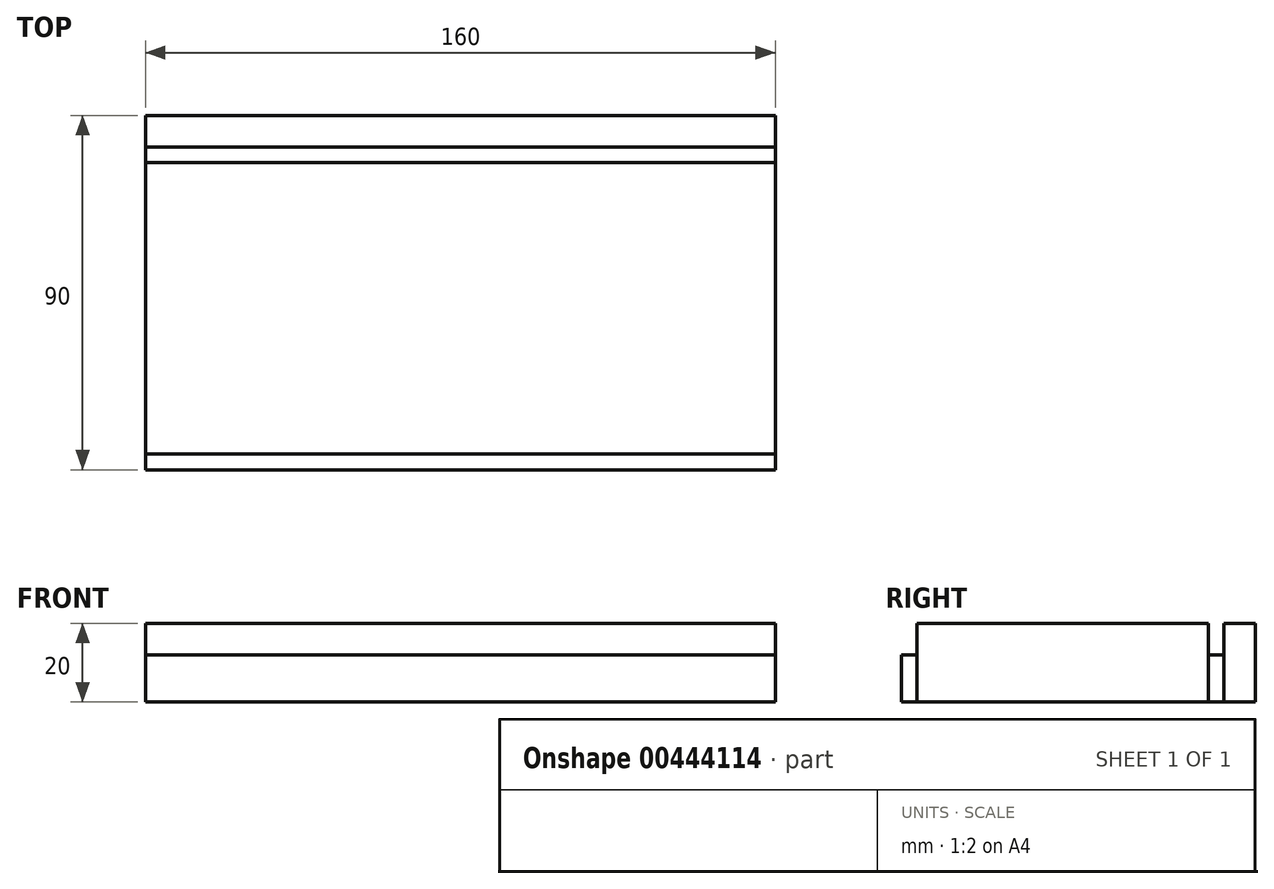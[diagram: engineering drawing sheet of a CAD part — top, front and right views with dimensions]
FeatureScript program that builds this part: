
annotation { "Feature Type Name" : "Feature", "Feature Type Description" : "" }
export const myFeature = defineFeature(function(context is Context, id is Id, definition is map)
    precondition{}
    {
        {
            var Q0;
            Q0=qCreatedBy(makeId("Top.planeOp"),FACE);
            var sketch = newSketch(context, id + "F0", { "sketchPlane" : qUnion([Q0])});
            skLineSegment(sketch, "E0.bottom", {"start": v(-78.73, 59.32) * mm, "end": v(81.27, 59.32) * mm});
            skLineSegment(sketch, "E0.top", {"start": v(-78.73, -30.68) * mm, "end": v(81.27, -30.68) * mm});
            skLineSegment(sketch, "E0.left", {"start": v(-78.73, 59.32) * mm, "end": v(-78.73, -30.68) * mm});
            skLineSegment(sketch, "E0.right", {"start": v(81.27, 59.32) * mm, "end": v(81.27, -30.68) * mm});
            skLineSegment(sketch, "E1.top", {"start": v(-78.73, 51.32) * mm, "end": v(81.27, 51.32) * mm});
            skLineSegment(sketch, "E1.left", {"start": v(-78.73, 59.32) * mm, "end": v(-78.73, 51.32) * mm});
            skLineSegment(sketch, "E1.right", {"start": v(81.27, 59.32) * mm, "end": v(81.27, 51.32) * mm});
            skLineSegment(sketch, "E2.top", {"start": v(-78.73, 47.32) * mm, "end": v(81.27, 47.32) * mm});
            skLineSegment(sketch, "E2.left", {"start": v(-78.73, 51.32) * mm, "end": v(-78.73, 47.32) * mm});
            skLineSegment(sketch, "E2.right", {"start": v(81.27, 51.32) * mm, "end": v(81.27, 47.32) * mm});
            skLineSegment(sketch, "E3.top", {"start": v(-78.73, -26.68) * mm, "end": v(81.27, -26.68) * mm});
            skLineSegment(sketch, "E3.left", {"start": v(-78.73, 47.32) * mm, "end": v(-78.73, -26.68) * mm});
            skLineSegment(sketch, "E3.right", {"start": v(81.27, 47.32) * mm, "end": v(81.27, -26.68) * mm});
            skLineSegment(sketch, "E4.left", {"start": v(-78.73, -26.68) * mm, "end": v(-78.73, -30.68) * mm});
            skLineSegment(sketch, "E4.right", {"start": v(81.27, -26.68) * mm, "end": v(81.27, -30.68) * mm});
            skSolve(sketch);
        }
        {
            var Q0;
            Q0=makeQuery(id+"F0.imprint","IMPRINT",FACE,{"disambiguationData":[TD([[makeQuery(id+"F0.imprint","IMPRINT",EDGE,{"derivedFrom":sQuery(id+"F0.wireOp",EDGE,"E0.bottom")}),-1.0]])]});
            var Q1;
            Q1=makeQuery(id+"F0.imprint","IMPRINT",FACE,{"disambiguationData":[TD([[makeQuery(id+"F0.imprint","IMPRINT",EDGE,{"derivedFrom":sQuery(id+"F0.wireOp",EDGE,"E2.top")}),-1.0]])]});
            extrude(context, id + "F1", {"entities" : qUnion([Q0, Q1]), "depth" : 20 * mm});
        }
        {
            var Q0;
            Q0=makeQuery(id+"F0.imprint","IMPRINT",FACE,{"disambiguationData":[TD([[makeQuery(id+"F0.imprint","IMPRINT",EDGE,{"derivedFrom":sQuery(id+"F0.wireOp",EDGE,"E1.top")}),-1.0]])]});
            var Q1;
            Q1=makeQuery(id+"F0.imprint","IMPRINT",FACE,{"disambiguationData":[TD([[makeQuery(id+"F0.imprint","IMPRINT",EDGE,{"derivedFrom":sQuery(id+"F0.wireOp",EDGE,"E0.top")}),1.0]])]});
            extrude(context, id + "F2", {"entities" : qUnion([Q0, Q1]), "depth" : 12 * mm});
        }
    });
